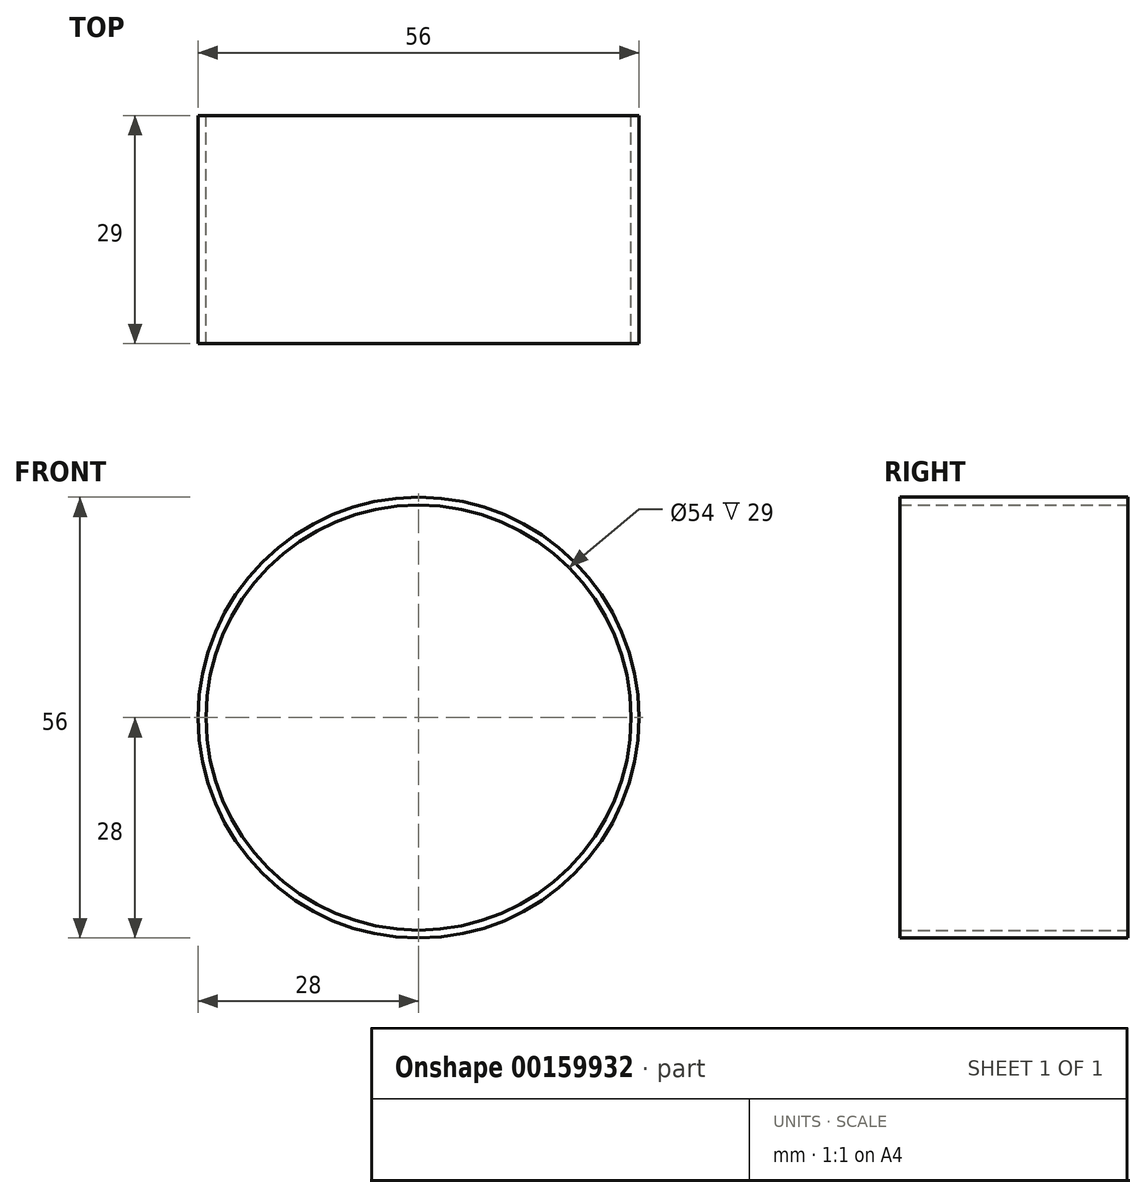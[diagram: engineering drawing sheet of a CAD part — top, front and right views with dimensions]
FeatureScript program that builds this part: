
annotation { "Feature Type Name" : "Feature", "Feature Type Description" : "" }
export const myFeature = defineFeature(function(context is Context, id is Id, definition is map)
    precondition{}
    {
        {
            var Q0;
            Q0=qCreatedBy(makeId("Front.planeOp"),FACE);
            var sketch = newSketch(context, id + "F0", { "sketchPlane" : qUnion([Q0])});
            skCircle(sketch, "E0", {"center": v(0, 0) * mm, "radius": 27 * mm});
            skCircle(sketch, "E1", {"center": v(0, 0) * mm, "radius": 28 * mm});
            skSolve(sketch);
        }
        {
            var Q0;
            Q0=makeQuery(id+"F0.imprint","IMPRINT",FACE,{"disambiguationData":[TD([[makeQuery(id+"F0.imprint","IMPRINT",EDGE,{"derivedFrom":sQuery(id+"F0.wireOp",EDGE,"E0")}),-1.0]])]});
            extrude(context, id + "F1", {"entities" : qUnion([Q0]), "depth" : 29 * mm});
        }
    });
